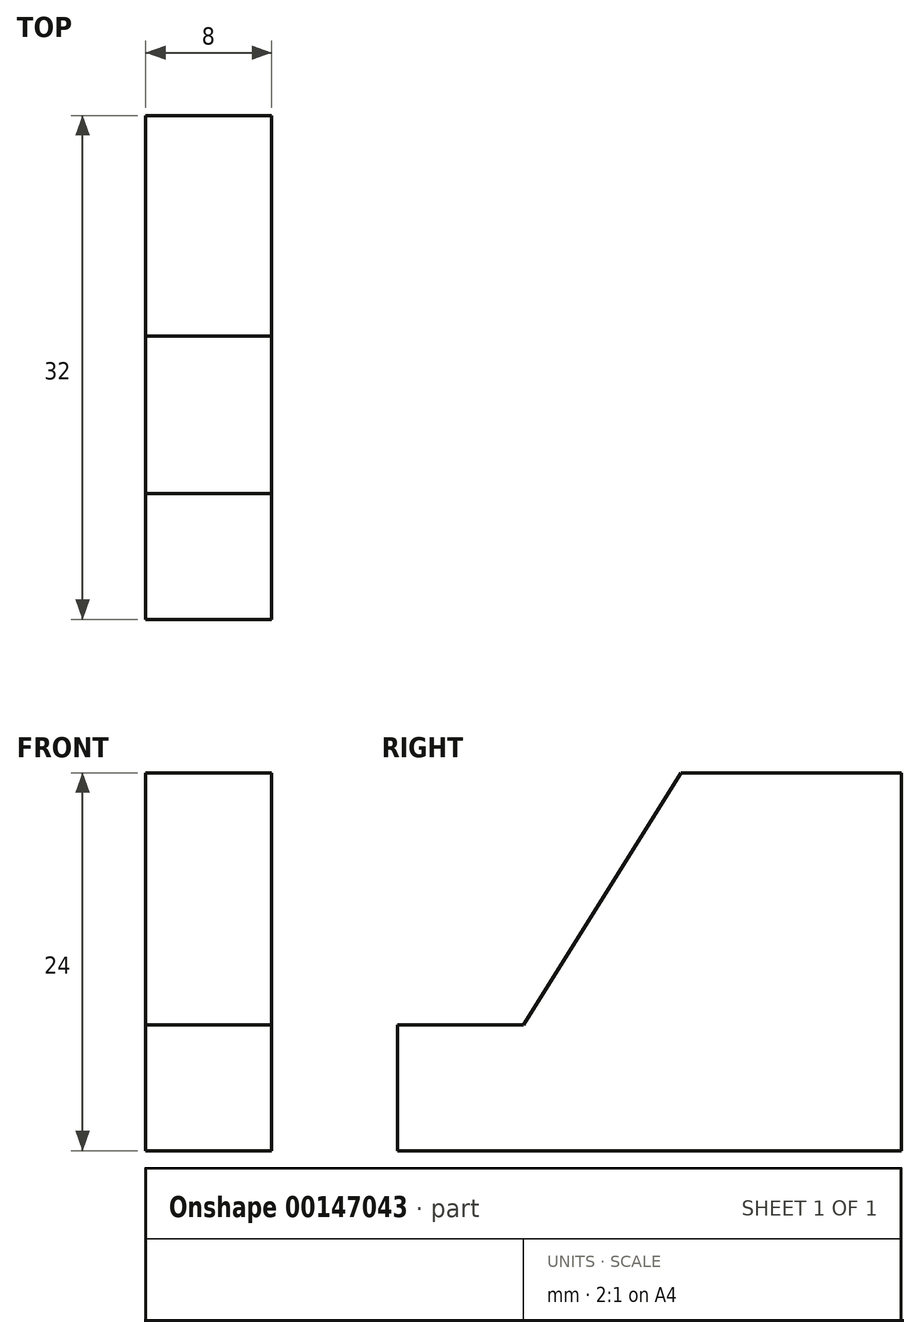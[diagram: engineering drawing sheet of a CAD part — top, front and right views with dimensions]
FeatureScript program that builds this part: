
annotation { "Feature Type Name" : "Feature", "Feature Type Description" : "" }
export const myFeature = defineFeature(function(context is Context, id is Id, definition is map)
    precondition{}
    {
        {
            var Q0;
            Q0=qCreatedBy(makeId("Right.planeOp"),FACE);
            var sketch = newSketch(context, id + "F0", { "sketchPlane" : qUnion([Q0])});
            skLineSegment(sketch, "E0", {"start": v(-21.46, 0) * mm, "end": v(10.54, 0) * mm});
            skLineSegment(sketch, "E1", {"start": v(-21.46, 0) * mm, "end": v(-21.46, 8) * mm});
            skLineSegment(sketch, "E2", {"start": v(-21.46, 8) * mm, "end": v(10.54, 8) * mm});
            skLineSegment(sketch, "E3", {"start": v(10.54, 8) * mm, "end": v(10.54, 0) * mm});
            skLineSegment(sketch, "E4", {"start": v(10.54, 8) * mm, "end": v(10.54, 24) * mm});
            skLineSegment(sketch, "E5", {"start": v(10.54, 24) * mm, "end": v(-3.46, 24) * mm});
            skLineSegment(sketch, "E6", {"start": v(10.54, 8) * mm, "end": v(-13.46, 8) * mm});
            skLineSegment(sketch, "E7", {"start": v(-13.46, 8) * mm, "end": v(-3.46, 24) * mm});
            skSolve(sketch);
        }
        {
            var Q0;
            Q0 = qSketchRegion(id + "F0", true);
            extrude(context, id + "F1", {"entities" : qUnion([Q0]), "depth" : 8 * mm});
        }
    });
